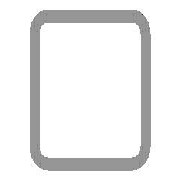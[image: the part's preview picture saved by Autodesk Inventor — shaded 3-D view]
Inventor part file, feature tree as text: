
AUTODESK INVENTOR PART (.ipt)
format: ipt  version: 2025 (Build 290162010, 162A)  size: 135,168 bytes
history: native  units: mm (DEFAULTED — no unit token found)
features: other x4, sketch x1, plane x1
ambient origin geometry x8: Origin, YZ Plane, XZ Plane, XY Plane, X Axis, Y Axis, Z Axis, Center Point
bodies: Solid1 (feature_tree), Body (feature_tree)
feature tree (6):
  parser-record x1  (decoder bookkeeping rows leaked as tree rows — omitted from the tree; the rows remain in map.json)
  other  "Driven Length"
  other  "Start Plane"
  other  "End Plane"
  sketch  "Sketch3"  dims[d3=912.375856mm d4=0.0mm d7=4.0mm d9=40.0mm d11=40.0mm d12=2.0mm d13=-0.0mm d14=912.375856mm d15=20.0mm d16=20.0mm d17=90.0deg d18=912.375856mm]
  plane  "Work Plane3"
